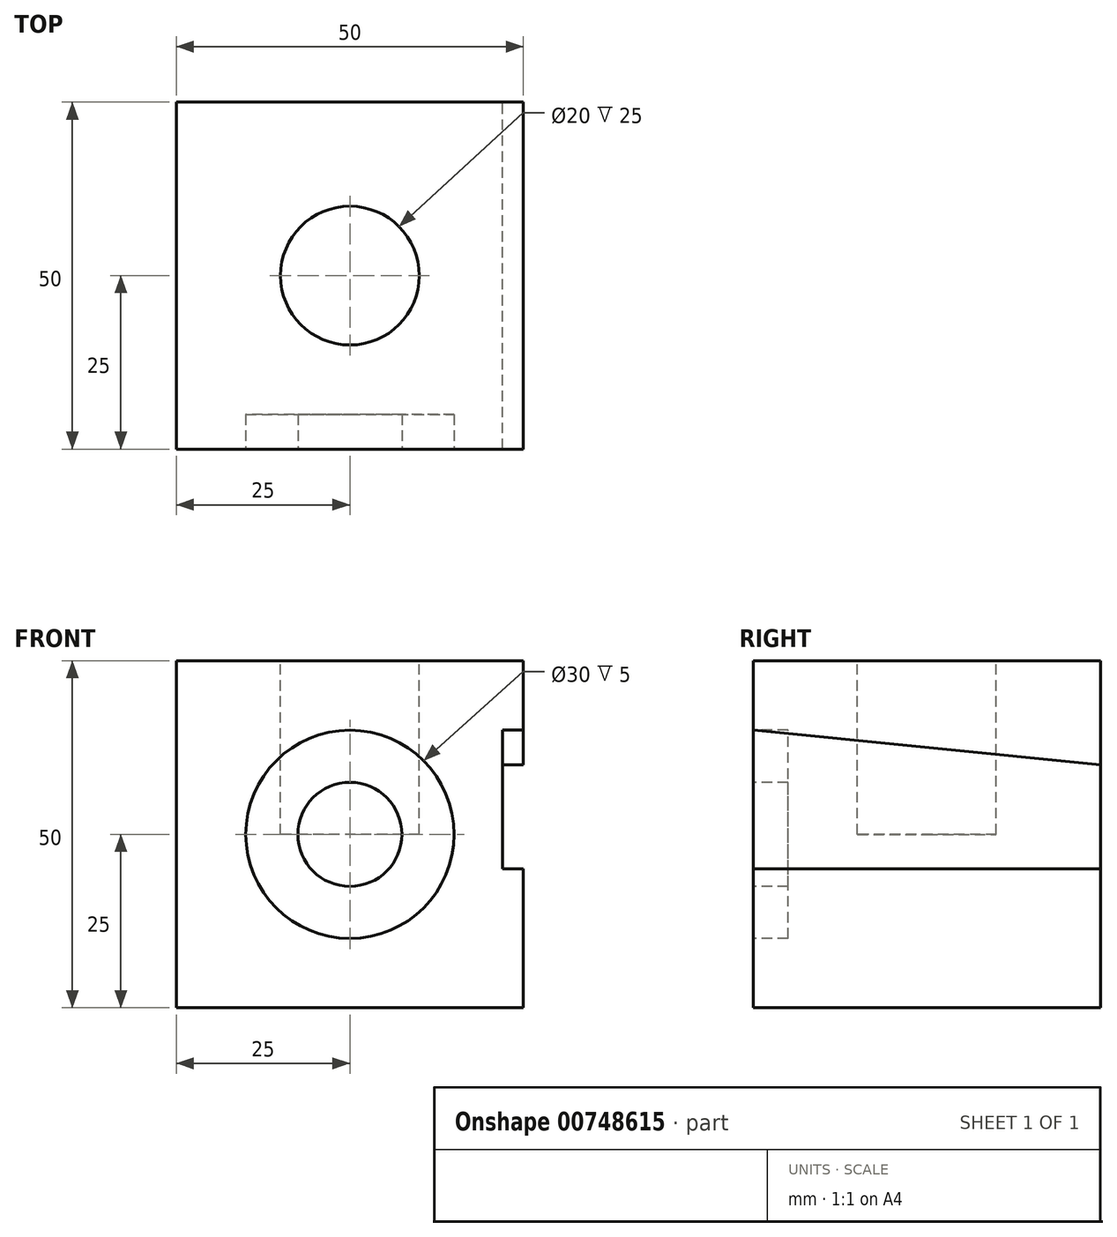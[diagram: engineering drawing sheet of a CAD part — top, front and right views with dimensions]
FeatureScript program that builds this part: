
annotation { "Feature Type Name" : "Feature", "Feature Type Description" : "" }
export const myFeature = defineFeature(function(context is Context, id is Id, definition is map)
    precondition{}
    {
        {
            var Q0;
            Q0=qCreatedBy(makeId("Top.planeOp"),FACE);
            var sketch = newSketch(context, id + "F0", { "sketchPlane" : qUnion([Q0])});
            skLineSegment(sketch, "E0.bottom", {"start": v(-25, 25) * mm, "end": v(25, 25) * mm});
            skLineSegment(sketch, "E0.top", {"start": v(-25, -25) * mm, "end": v(25, -25) * mm});
            skLineSegment(sketch, "E0.left", {"start": v(-25, 25) * mm, "end": v(-25, -25) * mm});
            skLineSegment(sketch, "E0.right", {"start": v(25, 25) * mm, "end": v(25, -25) * mm});
            skPoint(sketch, "E0.middle", {"position": v(0, 0) * mm});
            skSolve(sketch);
        }
        {
            var Q0;
            Q0=qSketchRegion(id+"F0",true);
            extrude(context, id + "F1", {"entities" : qUnion([Q0]), "depth" : 50 * mm, "offsetDistance" : 25 * mm});
        }
        {
            var Q0;
            Q0=makeQuery(id+"F1.opExtrude","CAP_FACE",FACE,{"disambiguationData":[OSD([sQuery(id+"F0.wireOp",EDGE,"E0.bottom"),sQuery(id+"F0.wireOp",EDGE,"E0.top"),sQuery(id+"F0.wireOp",EDGE,"E0.left"),sQuery(id+"F0.wireOp",EDGE,"E0.right")])],"isStart":false});
            var sketch = newSketch(context, id + "F2", { "sketchPlane" : qUnion([Q0])});
            skCircle(sketch, "E1", {"center": v(0, 0) * mm, "radius": 10 * mm});
            skSolve(sketch);
        }
        {
            var Q0;
            Q0=qSketchRegion(id+"F2",true);
            extrude(context, id + "F3", {"entities" : qUnion([Q0]), "operationType" : NewBodyOperationType.REMOVE, "oppositeDirection" : true, "depth" : 25 * mm, "offsetDistance" : 25 * mm});
        }
        {
            var Q0;
            Q0=makeQuery(id+"F1.opExtrude","SWEPT_FACE",FACE,{"disambiguationData":[OSD([sQuery(id+"F0.wireOp",EDGE,"E0.top")])]});
            var sketch = newSketch(context, id + "F4", { "sketchPlane" : qUnion([Q0])});
            skLineSegment(sketch, "E2", {"start": v(-25, 25) * mm, "end": v(25, 25) * mm, "construction": true});
            skCircle(sketch, "E3", {"center": v(0, 25) * mm, "radius": 7.5 * mm});
            skCircle(sketch, "E4", {"center": v(0, 25) * mm, "radius": 15 * mm});
            skSolve(sketch);
        }
        {
            var Q0;
            Q0=makeQuery(id+"F4.imprint","IMPRINT",FACE,{"disambiguationData":[TD([[makeQuery(id+"F4.imprint","IMPRINT",EDGE,{"derivedFrom":sQuery(id+"F4.wireOp",EDGE,"E3")}),-1.0]])]});
            var Q1;
            Q1=sQuery(id+"F4.wireOp",EDGE,"E3");
            var Q2;
            Q2=sQuery(id+"F4.wireOp",EDGE,"E4");
            extrude(context, id + "F5", {"entities" : qUnion([Q0]), "operationType" : NewBodyOperationType.REMOVE, "surfaceEntities" : qUnion([Q1, Q2]), "oppositeDirection" : true, "depth" : 5 * mm, "offsetDistance" : 25 * mm});
        }
        {
            var Q0;
            Q0=makeQuery(id+"F1.opExtrude","SWEPT_FACE",FACE,{"disambiguationData":[OSD([sQuery(id+"F0.wireOp",EDGE,"E0.right")])]});
            var sketch = newSketch(context, id + "F6", { "sketchPlane" : qUnion([Q0])});
            skLineSegment(sketch, "E5", {"start": v(-25, 40) * mm, "end": v(25, 35) * mm});
            skLineSegment(sketch, "E6", {"start": v(25, 35) * mm, "end": v(25, 20) * mm});
            skLineSegment(sketch, "E7", {"start": v(25, 20) * mm, "end": v(-25, 20) * mm});
            skLineSegment(sketch, "E8", {"start": v(-25, 20) * mm, "end": v(-25, 40) * mm});
            skSolve(sketch);
        }
        {
            var Q0;
            Q0=qSketchRegion(id+"F6",true);
            extrude(context, id + "F7", {"entities" : qUnion([Q0]), "operationType" : NewBodyOperationType.REMOVE, "oppositeDirection" : true, "depth" : 3 * mm, "offsetDistance" : 25 * mm});
        }
    });
